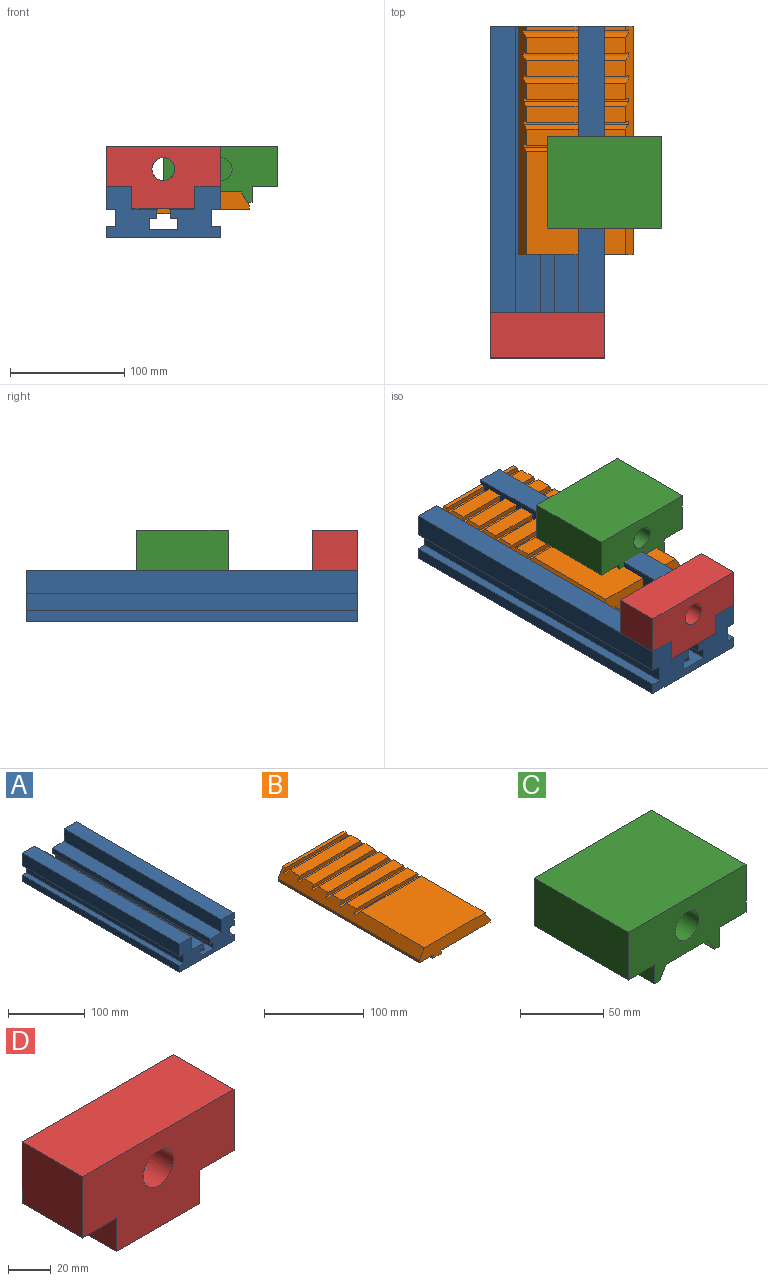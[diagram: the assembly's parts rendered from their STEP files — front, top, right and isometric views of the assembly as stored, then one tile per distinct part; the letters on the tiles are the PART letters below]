
ASSEMBLY  parts=4 mates=8
PART A: 28 faces, bbox 100x290x45 mm
  f0: plane 290x22.5mm, normal (0,0,1), area 6525mm2, adj f21,f22,f23,f24
  f1: plane 290x22.5mm, normal (0,0,1), area 6525mm2, adj f20,f21,f23,f25
  f2: plane 290x21.5mm, normal (0,0,1), area 6235mm2, adj f3,f21,f22,f23
  f3: plane 290x8mm, normal (1,0,0), area 2320mm2, adj f2,f4,f21,f23
  f4: plane 290x6.5mm, normal (0,0,-1), area 1885mm2, adj f3,f5,f21,f23
  f5: plane 290x10mm, normal (1,0,0), area 2900mm2, adj f4,f6,f21,f23
  f6: plane 290x25mm, normal (0,0,1), area 7173mm2, adj f5,f7,f21,f23,f26,f27
  f7: plane 290x10mm, normal (-1,0,0), area 2900mm2, adj f6,f8,f21,f23
  f8: plane 290x6.5mm, normal (0,0,-1), area 1885mm2, adj f7,f9,f21,f23
  f9: plane 290x8mm, normal (-1,0,0), area 2320mm2, adj f8,f10,f21,f23
  f10: plane 290x21.5mm, normal (0,0,1), area 6235mm2, adj f9,f20,f21,f23
  f11: plane 290x8mm, normal (0,0,-1), area 2320mm2, adj f12,f21,f23,f25
  f12: plane 290x15mm, normal (1,0,0), area 4350mm2, adj f11,f13,f21,f23
  f13: plane 290x8mm, normal (0,0,1), area 2320mm2, adj f12,f14,f21,f23
  f14: plane 290x10mm, normal (1,0,0), area 2900mm2, adj f13,f15,f21,f23
  f15: plane 290x100mm, normal (0,0,-1), area 28923mm2, adj f14,f16,f21,f23,f26,f27
  f16: plane 290x10mm, normal (-1,0,0), area 2900mm2, adj f15,f17,f21,f23
  f17: plane 290x8mm, normal (0,0,1), area 2320mm2, adj f16,f18,f21,f23
  f18: plane 290x15mm, normal (-1,0,0), area 4350mm2, adj f17,f19,f21,f23
  f19: plane 290x8mm, normal (0,0,-1), area 2320mm2, adj f18,f21,f23,f24
  f20: plane 290x20mm, normal (-1,0,0), area 5800mm2, adj f1,f10,f21,f23
  f21: plane 100x45mm, normal (0,1,0), area 2814mm2, adj f0,f1,f2,f3,f4,f5,f6,f7
  f22: plane 290x20mm, normal (1,0,0), area 5800mm2, adj f0,f2,f21,f23
  f23: plane 100x45mm, normal (0,-1,0), area 2814mm2, adj f0,f1,f2,f3,f4,f5,f6,f7
  f24: plane 290x20mm, normal (-1,0,0), area 5800mm2, adj f0,f19,f21,f23
  f25: plane 290x20mm, normal (1,0,0), area 5800mm2, adj f1,f11,f21,f23
  f26: cylinder r=3.5mm len=7mm, axis (0,0,-1), area 153.9mm2, adj f6,f15
  f27: cylinder r=3.5mm len=7mm, axis (0,0,-1), area 153.9mm2, adj f6,f15
PART B: 42 faces, bbox 100x200x19 mm
  f0: plane 200x67.59mm, normal (0,0,-1), area 13517.2mm2, adj f1,f2,f11,f40
  f1: plane 100x19mm, normal (0,-1,0), area 1460.9mm2, adj f0,f3,f10,f11,f12,f31,f32,f33
  f2: plane 100x19mm, normal (0,1,0), area 1460.9mm2, adj f0,f3,f9,f11,f12,f31,f32,f33
  f3: plane 200x2.59mm, normal (1,0,0), area 517.2mm2, adj f1,f2,f34,f41
  f4: plane 86.14x14mm, normal (0,0,1), area 1206mm2, adj f27,f28,f32,f33
  f5: plane 86.14x14mm, normal (0,0,1), area 1206mm2, adj f24,f25,f32,f33
  f6: plane 86.14x14mm, normal (0,0,1), area 1206mm2, adj f21,f22,f32,f33
  f7: plane 86.14x14mm, normal (0,0,1), area 1206mm2, adj f18,f19,f32,f33
  f8: plane 86.14x14mm, normal (0,0,1), area 1206mm2, adj f15,f16,f32,f33
  f9: plane 86.14x4mm, normal (0,0,1), area 344.6mm2, adj f2,f13,f32,f33
  f10: plane 90x86.14mm, normal (0,0,1), area 7752.9mm2, adj f1,f30,f32,f33
  f11: plane 200x3mm, normal (1,0,0), area 600mm2, adj f0,f1,f2,f32
  f12: plane 200x3mm, normal (-1,0,0), area 600mm2, adj f1,f2,f31,f33
  f13: plane 91.92x5mm, normal (0,-0.99,-0.14), area 449.5mm2, adj f9,f14,f32,f33
  f14: plane 91.92x3mm, normal (0,0,1), area 275.8mm2, adj f13,f15,f32,f33
  f15: plane 91.92x5mm, normal (0,0.8,0.6), area 553.9mm2, adj f8,f14,f32,f33
  f16: plane 91.92x5mm, normal (0,-0.99,-0.14), area 449.5mm2, adj f8,f17,f32,f33
  f17: plane 91.92x3mm, normal (0,0,1), area 275.8mm2, adj f16,f18,f32,f33
  f18: plane 91.92x5mm, normal (0,0.8,0.6), area 553.9mm2, adj f7,f17,f32,f33
  f19: plane 91.92x5mm, normal (0,-0.99,-0.14), area 449.5mm2, adj f7,f20,f32,f33
  f20: plane 91.92x3mm, normal (0,0,1), area 275.8mm2, adj f19,f21,f32,f33
  f21: plane 91.92x5mm, normal (0,0.8,0.6), area 553.9mm2, adj f6,f20,f32,f33
  f22: plane 91.92x5mm, normal (0,-0.99,-0.14), area 449.5mm2, adj f6,f23,f32,f33
  f23: plane 91.92x3mm, normal (0,0,1), area 275.8mm2, adj f22,f24,f32,f33
  f24: plane 91.92x5mm, normal (0,0.8,0.6), area 553.9mm2, adj f5,f23,f32,f33
  f25: plane 91.92x5mm, normal (0,-0.99,-0.14), area 449.5mm2, adj f5,f26,f32,f33
  f26: plane 91.92x3mm, normal (0,0,1), area 275.8mm2, adj f25,f27,f32,f33
  f27: plane 91.92x5mm, normal (0,0.8,0.6), area 553.9mm2, adj f4,f26,f32,f33
  f28: plane 91.92x5mm, normal (0,-0.99,-0.14), area 449.5mm2, adj f4,f29,f32,f33
  f29: plane 91.92x3mm, normal (0,0,1), area 275.8mm2, adj f28,f30,f32,f33
  f30: plane 91.92x5mm, normal (0,0.8,0.6), area 553.9mm2, adj f10,f29,f32,f33
  f31: plane 200x17.59mm, normal (0,0,-1), area 3517.2mm2, adj f1,f2,f12,f36
  f32: plane 200x12mm, normal (0.87,0,0.5), area 2615.4mm2, adj f1,f2,f4,f5,f6,f7,f8,f9
  f33: plane 200x12mm, normal (-0.87,0,0.5), area 2615.4mm2, adj f1,f2,f4,f5,f6,f7,f8,f9
  f34: plane 200x12mm, normal (0,0,-1), area 2400mm2, adj f1,f2,f3,f35
  f35: plane 200x2.59mm, normal (-1,0,0), area 517.2mm2, adj f1,f2,f34,f38
  f36: plane 200x1.06mm, normal (0.71,0,-0.71), area 300mm2, adj f1,f2,f31,f37
  f37: plane 200x1.41mm, normal (-0.71,0,-0.71), area 400mm2, adj f1,f2,f36,f38
  f38: plane 200x1.06mm, normal (-0.71,0,0.71), area 300mm2, adj f1,f2,f35,f37
  f39: plane 200x1.41mm, normal (0.71,0,-0.71), area 400mm2, adj f1,f2,f40,f41
  f40: plane 200x1.06mm, normal (-0.71,0,-0.71), area 300mm2, adj f0,f1,f2,f39
  f41: plane 200x1.06mm, normal (0.71,0,0.71), area 300mm2, adj f1,f2,f3,f39
PART C: 16 faces, bbox 100x80x49 mm
  f0: plane 80x35mm, normal (-1,0,0), area 2800mm2, adj f1,f6,f7,f8
  f1: plane 80x22.5mm, normal (0,0,-1), area 1800mm2, adj f0,f2,f7,f8
  f2: plane 80x14mm, normal (-1,0,0), area 1120mm2, adj f1,f3,f7,f8
  f3: plane 80x4.23mm, normal (0,0,-1), area 338.6mm2, adj f2,f4,f7,f8
  f4: plane 80x9.5mm, normal (0.87,0,-0.5), area 877.6mm2, adj f3,f5,f7,f8
  f5: plane 80x35.57mm, normal (0,0,-1), area 2845.3mm2, adj f4,f7,f8,f13
  f6: plane 100x80mm, normal (0,0,1), area 8000mm2, adj f0,f7,f8,f9
  f7: plane 100x49mm, normal (0,-1,0), area 3565.9mm2, adj f0,f1,f2,f3,f4,f5,f6,f9
  f8: plane 100x49mm, normal (0,1,0), area 3880mm2, adj f0,f1,f2,f3,f4,f5,f6,f9
  f9: plane 80x35mm, normal (1,0,0), area 2800mm2, adj f6,f7,f8,f10
  f10: plane 80x22.5mm, normal (0,0,-1), area 1800mm2, adj f7,f8,f9,f11
  f11: plane 80x14mm, normal (1,0,0), area 1120mm2, adj f7,f8,f10,f12
  f12: plane 80x4.23mm, normal (0,0,-1), area 338.6mm2, adj f7,f8,f11,f13
  f13: plane 80x9.5mm, normal (-0.87,0,-0.5), area 877.6mm2, adj f5,f7,f8,f12
  f14: cylinder r=10mm len=25mm, axis (0,-1,0), area 1570.8mm2, adj f7,f15
  f15: plane 20x20mm, normal (0,-1,0), area 314.2mm2, adj f14
PART D: 14 faces, bbox 100x40x54 mm
  f0: plane 100x54mm, normal (0,1,0), area 4230.8mm2, adj f1,f2,f3,f4,f5,f7,f9,f12
  f1: plane 40x19mm, normal (-1,0,0), area 760mm2, adj f0,f6,f12,f13
  f2: plane 40x19mm, normal (1,0,0), area 760mm2, adj f0,f3,f6,f13
  f3: plane 40x22.5mm, normal (0,0,-1), area 900mm2, adj f0,f2,f4,f6
  f4: plane 40x35mm, normal (1,0,0), area 1286.9mm2, adj f0,f3,f6,f7,f8
  f5: plane 40x35mm, normal (-1,0,0), area 1400mm2, adj f0,f6,f7,f12
  f6: plane 100x54mm, normal (0,-1,0), area 4230.8mm2, adj f1,f2,f3,f4,f5,f7,f9,f12
  f7: plane 100x40mm, normal (0,0,1), area 4000mm2, adj f0,f4,f5,f6
  f8: cylinder r=6mm len=42mm, axis (1,0,0), area 1544.7mm2, adj f4,f9
  f9: cylinder r=10mm len=40mm, axis (0,-1,0), area 2275.4mm2, adj f0,f6,f8,f11
  f10: plane 12x12mm, normal (1,0,0), area 113.1mm2, adj f11
  f11: cylinder r=6mm len=12mm, axis (1,0,0), area 225.1mm2, adj f9,f10
  f12: plane 40x22.5mm, normal (0,0,-1), area 900mm2, adj f0,f1,f5,f6
  f13: plane 55x40mm, normal (0,0,-1), area 2200mm2, adj f0,f1,f2,f6
PLACE A t=(2.66,-52.26,71.01)mm fixed
PLACE B t=(88.53,237.74,66.72)mm
PLACE C t=(50,141.19,0)mm
PLACE D t=(2.66,-52.26,71.01)mm
MATE planar B.f2 <-> A.f21  axis (0,1,0) through (76.9,237.74,103.02)mm
MATE planar D.f6 <-> A.f23  axis (0,-1,0) through (52.66,-52.26,127.03)mm
MATE planar C.f13 <-> B.f32  axis (-0.87,0,-0.5) through (123.18,101.19,106.76)mm
MATE planar D.f2 <-> A.f20  axis (1,0,0) through (80.16,-32.26,106.51)mm
MATE planar C.f1 <-> A.f0  axis (0,0,-1) through (52.66,101.19,116.01)mm
MATE planar B.f31 <-> A.f2  axis (0,0,-1) through (27.66,237.74,96.01)mm
MATE planar B.f35 <-> A.f3  axis (-1,0,0) through (46.66,137.74,93.31)mm
MATE planar D.f3 <-> A.f0  axis (0,0,-1) through (91.41,-32.26,116.01)mm
